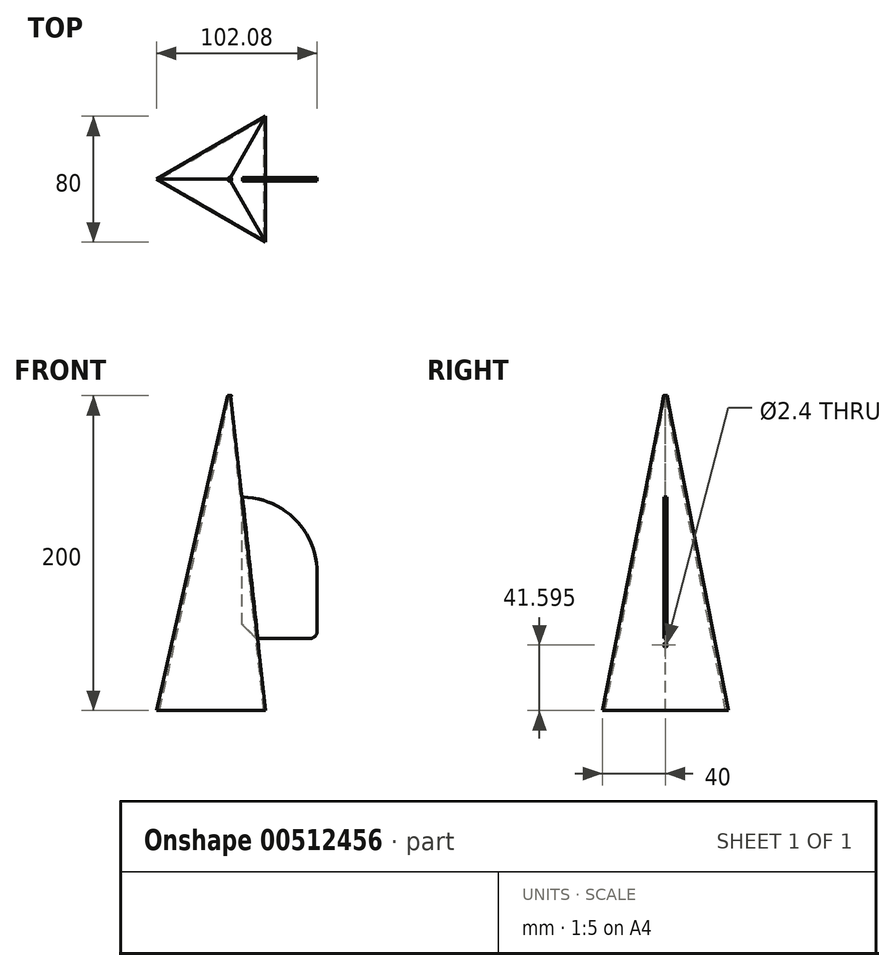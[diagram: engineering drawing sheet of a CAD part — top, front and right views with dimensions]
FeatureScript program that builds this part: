
annotation { "Feature Type Name" : "Feature", "Feature Type Description" : "" }
export const myFeature = defineFeature(function(context is Context, id is Id, definition is map)
    precondition{}
    {
        {
            var Q0;
            Q0=qCreatedBy(makeId("Top.planeOp"),FACE);
            cPlane(context, id + "F0", {"entities" : qUnion([Q0]), "cplaneType" : CPlaneType.OFFSET, "offset" : 200 * mm, "width" : 152.4 * mm, "height" : 152.4 * mm});
        }
        {
            var Q0;
            Q0=qCreatedBy(makeId("Top.planeOp"),FACE);
            var sketch = newSketch(context, id + "F1", { "sketchPlane" : qUnion([Q0])});
            skLineSegment(sketch, "E0", {"start": v(0, 40) * mm, "end": v(-69.28, 0) * mm});
            skLineSegment(sketch, "E1", {"start": v(-69.28, 0) * mm, "end": v(0, -40) * mm});
            skLineSegment(sketch, "E2", {"start": v(0, -40) * mm, "end": v(0, 40) * mm});
            skSolve(sketch);
        }
        {
            var Q0;
            Q0=qCreatedBy(id+"F0.planeOp",FACE);
            var sketch = newSketch(context, id + "F2", { "sketchPlane" : qUnion([Q0])});
            skCircle(sketch, "E3", {"center": v(-22.73, 0) * mm, "radius": 1.26 * mm});
            skSolve(sketch);
        }
        {
            var Q0;
            Q0=makeQuery(id+"F1.imprint","IMPRINT",FACE,{"disambiguationData":[TD([[makeQuery(id+"F1.imprint","IMPRINT",EDGE,{"derivedFrom":sQuery(id+"F1.wireOp",EDGE,"E0")}),1.0]])]});
            var Q1;
            Q1=makeQuery(id+"F2.imprint","IMPRINT",FACE,{"disambiguationData":[TD([[makeQuery(id+"F2.imprint","IMPRINT",EDGE,{"derivedFrom":sQuery(id+"F2.wireOp",EDGE,"E3")}),1.0]])]});
            loft(context, id + "F3", {"sheetProfilesArray" : [{ "sheetProfileEntities" : qUnion([Q0]) }, { "sheetProfileEntities" : qUnion([Q1]) }]});
        }
        {
            var Q0;
            Q0=makeQuery(id+"F3.opLoft","CAP_FACE",FACE,{"disambiguationData":[OSD([makeQuery(id+"F1.imprint","IMPRINT",FACE,{"disambiguationData":[TD([[makeQuery(id+"F1.imprint","IMPRINT",EDGE,{"derivedFrom":sQuery(id+"F1.wireOp",EDGE,"E0")}),1.0]])]})])],"isStart":true});
            shell(context, id + "F4", {"entities" : qUnion([Q0]), "thickness" : 1 * mm});
        }
        {
            var Q0;
            Q0=qCreatedBy(makeId("Right.planeOp"),FACE);
            var sketch = newSketch(context, id + "F5", { "sketchPlane" : qUnion([Q0])});
            skLineSegment(sketch, "E4.bottom", {"start": v(1, 45.7) * mm, "end": v(-1, 45.7) * mm});
            skLineSegment(sketch, "E4.top", {"start": v(1, 135.7) * mm, "end": v(-1, 135.7) * mm});
            skLineSegment(sketch, "E4.left", {"start": v(1, 45.7) * mm, "end": v(1, 135.7) * mm});
            skLineSegment(sketch, "E4.right", {"start": v(-1, 45.7) * mm, "end": v(-1, 135.7) * mm});
            skPoint(sketch, "E4.middle", {"position": v(0, 90.7) * mm});
            skSolve(sketch);
        }
        {
            var Q0;
            Q0=makeQuery(id+"F5.imprint","IMPRINT",FACE,{"disambiguationData":[TD([[makeQuery(id+"F5.imprint","IMPRINT",EDGE,{"derivedFrom":sQuery(id+"F5.wireOp",EDGE,"E4.bottom")}),-1.0]])]});
            var Q1;
            {var subQ0=sQuery(id+"F2.wireOp",EDGE,"E3");var subQ1=sQuery(id+"F1.wireOp",EDGE,"E2");var subQ2=sQuery(id+"F1.wireOp",EDGE,"E1");var subQ3=sQuery(id+"F1.wireOp",EDGE,"E0");Q1=makeQuery(id+"F3.opLoft","SWEPT_FACE",FACE,{"disambiguationData":[OSD([subQ3,subQ2,subQ1,subQ0]),TDD([makeQuery(id+"F1.imprint","INTERSECT",VERTEX,{"derivedFrom":[subQ3,subQ1]}),makeQuery(id+"F1.imprint","INTERSECT",VERTEX,{"derivedFrom":[subQ3,subQ2]}),makeQuery(id+"F1.imprint","INTERSECT",VERTEX,{"derivedFrom":[subQ2,subQ1]}),makeQuery(id+"F1.imprint","IMPRINT",EDGE,{"derivedFrom":subQ1}),makeQuery(id+"F2.imprint","IMPRINT",EDGE,{"derivedFrom":subQ0})])]});}
            extrude(context, id + "F6", {"entities" : qUnion([Q0]), "operationType" : NewBodyOperationType.ADD, "endBound" : BoundingType.SYMMETRIC, "endBoundEntityFace" : qUnion([Q1]), "depth" : 29.6 * mm});
        }
        {
            var Q0;
            Q0=makeQuery(id+"F6.opExtrude","CAP_FACE",FACE,{"disambiguationData":[OSD([sQuery(id+"F5.wireOp",EDGE,"E4.bottom"),sQuery(id+"F5.wireOp",EDGE,"E4.top"),sQuery(id+"F5.wireOp",EDGE,"E4.left"),sQuery(id+"F5.wireOp",EDGE,"E4.right")])],"isStart":false});
            var sketch = newSketch(context, id + "F7", { "sketchPlane" : qUnion([Q0])});
            skLineSegment(sketch, "E5.bottom", {"start": v(-1, 135.7) * mm, "end": v(1, 135.7) * mm});
            skLineSegment(sketch, "E5.top", {"start": v(-1, 45.7) * mm, "end": v(1, 45.7) * mm});
            skLineSegment(sketch, "E5.left", {"start": v(-1, 135.7) * mm, "end": v(-1, 45.7) * mm});
            skLineSegment(sketch, "E5.right", {"start": v(1, 135.7) * mm, "end": v(1, 45.7) * mm});
            skSolve(sketch);
        }
        {
            var Q0;
            Q0 = qSketchRegion(id + "F7", true);
            extrude(context, id + "F8", {"entities" : qUnion([Q0]), "operationType" : NewBodyOperationType.ADD, "depth" : 18 * mm});
        }
        {
            var Q0;
            Q0=makeQuery(id+"F8.opExtrude","CAP_EDGE",EDGE,{"disambiguationData":[OSD([sQuery(id+"F7.wireOp",EDGE,"E5.bottom")])],"isStart":false});
            fillet(context, id + "F9", {"entities" : qUnion([Q0]), "radius" : 48.28 * mm, "tangentPropagation" : true, "allowEdgeOverflow" : false});
        }
        {
            var Q0;
            Q0=makeQuery(id+"F8.opExtrude","CAP_EDGE",EDGE,{"disambiguationData":[OSD([sQuery(id+"F7.wireOp",EDGE,"E5.top")])],"isStart":false});
            fillet(context, id + "F10", {"entities" : qUnion([Q0]), "radius" : 5 * mm, "tangentPropagation" : true, "allowEdgeOverflow" : false});
        }
        {
            var Q0;
            Q0=qCreatedBy(makeId("Right.planeOp"),FACE);
            var sketch = newSketch(context, id + "F11", { "sketchPlane" : qUnion([Q0])});
            skLineSegment(sketch, "E6.bottom", {"start": v(-1, 9.16) * mm, "end": v(1, 9.16) * mm, "construction": true});
            skLineSegment(sketch, "E6.top", {"start": v(-1, 44.16) * mm, "end": v(1, 44.16) * mm, "construction": true});
            skLineSegment(sketch, "E6.left", {"start": v(-1, 9.16) * mm, "end": v(-1, 44.16) * mm, "construction": true});
            skLineSegment(sketch, "E6.right", {"start": v(1, 9.16) * mm, "end": v(1, 44.16) * mm, "construction": true});
            skPoint(sketch, "E6.middle", {"position": v(0, 26.66) * mm});
            skLineSegment(sketch, "E7", {"start": v(-3.84, 10.52) * mm, "end": v(6.73, 10.52) * mm, "construction": true});
            skPoint(sketch, "E8.center.orphan", {"position": v(0, 11.72) * mm});
            skCircle(sketch, "E9", {"center": v(0, 41.6) * mm, "radius": 1.2 * mm});
            skSolve(sketch);
        }
        {
            var Q0;
            Q0=makeQuery(id+"F11.imprint","IMPRINT",FACE,{"disambiguationData":[TD([[makeQuery(id+"F11.imprint","IMPRINT",EDGE,{"derivedFrom":sQuery(id+"F11.wireOp",EDGE,"E9")}),1.0]])]});
            var Q1;
            {var subQ0=sQuery(id+"F2.wireOp",EDGE,"E3");var subQ1=sQuery(id+"F1.wireOp",EDGE,"E2");var subQ2=sQuery(id+"F1.wireOp",EDGE,"E1");var subQ3=sQuery(id+"F1.wireOp",EDGE,"E0");Q1=makeQuery(id+"F4.opShell","OFFSET_FACE",FACE,{"disambiguationData":[OSD([subQ3,subQ2,subQ1,subQ0]),TDD([makeQuery(id+"F3.opLoft","SWEPT_FACE",FACE,{"disambiguationData":[OSD([subQ3,subQ2,subQ1,subQ0]),TDD([makeQuery(id+"F1.imprint","INTERSECT",VERTEX,{"derivedFrom":[subQ3,subQ1]}),makeQuery(id+"F1.imprint","INTERSECT",VERTEX,{"derivedFrom":[subQ3,subQ2]}),makeQuery(id+"F1.imprint","INTERSECT",VERTEX,{"derivedFrom":[subQ2,subQ1]}),makeQuery(id+"F1.imprint","IMPRINT",EDGE,{"derivedFrom":subQ1}),makeQuery(id+"F2.imprint","IMPRINT",EDGE,{"derivedFrom":subQ0})])]})])]});}
            extrude(context, id + "F12", {"entities" : qUnion([Q0]), "operationType" : NewBodyOperationType.REMOVE, "endBound" : BoundingType.UP_TO_SURFACE, "oppositeDirection" : true, "endBoundEntityFace" : qUnion([Q1]), "depth" : 25 * mm});
        }
        {
            var Q0;
            Q0=makeQuery(id+"F6.opExtrude","CAP_EDGE",EDGE,{"disambiguationData":[OSD([sQuery(id+"F5.wireOp",EDGE,"E4.bottom")])],"isStart":true});
            chamfer(context, id + "F13", {"entities" : qUnion([Q0]), "width" : 9 * mm, "tangentPropagation" : true});
        }
    });
